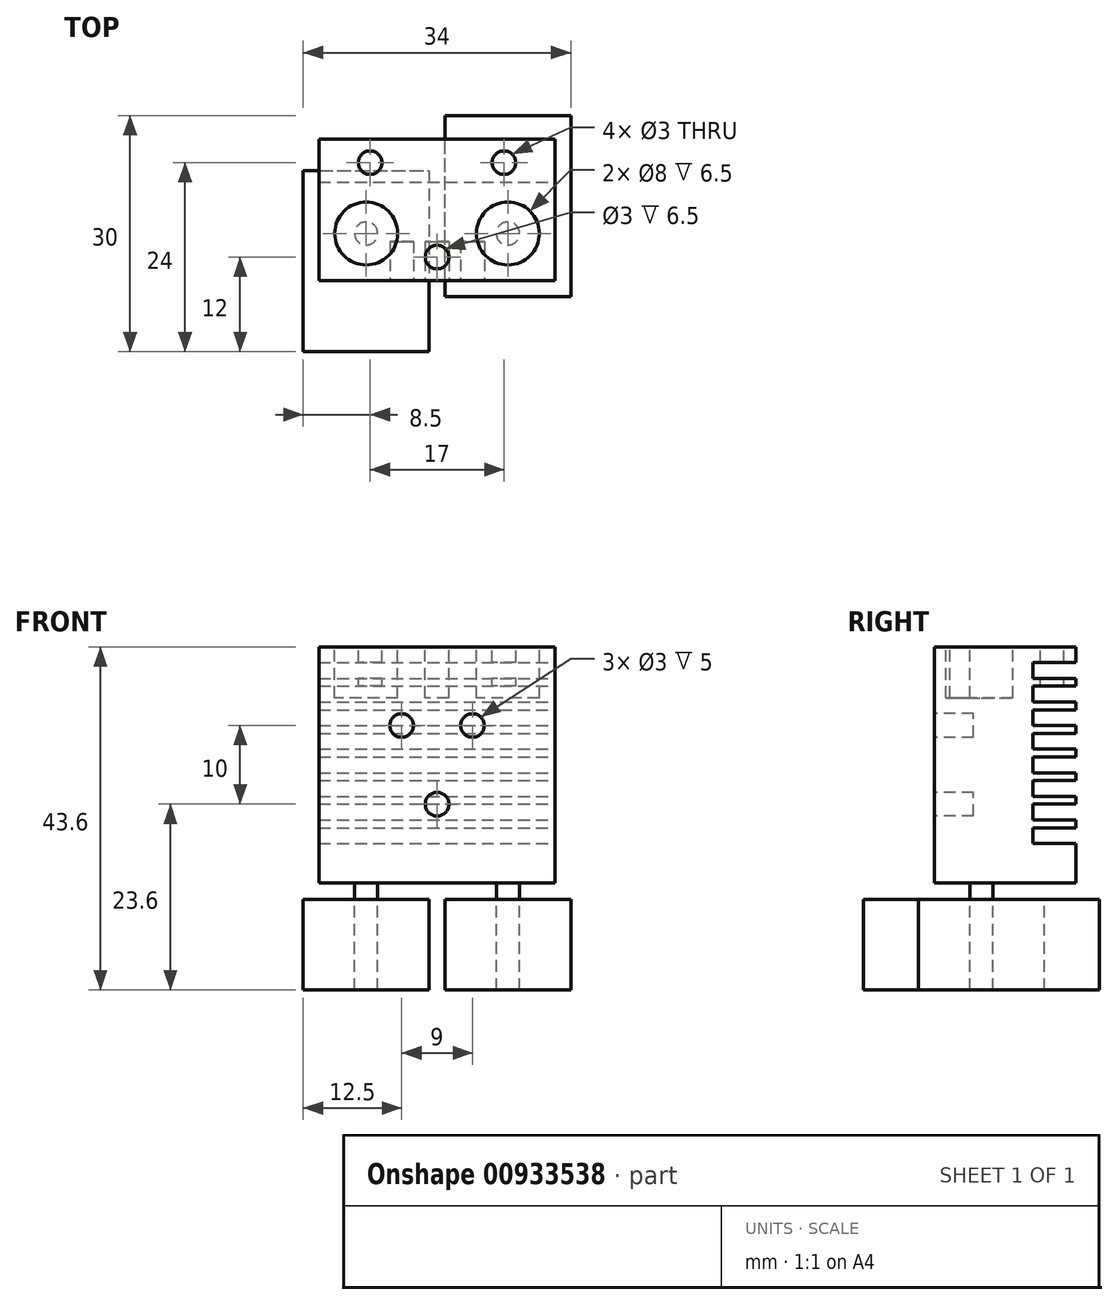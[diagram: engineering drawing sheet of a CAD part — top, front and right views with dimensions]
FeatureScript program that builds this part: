
annotation { "Feature Type Name" : "Feature", "Feature Type Description" : "" }
export const myFeature = defineFeature(function(context is Context, id is Id, definition is map)
    precondition{}
    {
        {
            var Q0;
            Q0=qCreatedBy(makeId("Front.planeOp"),FACE);
            var sketch = newSketch(context, id + "F0", { "sketchPlane" : qUnion([Q0])});
            skLineSegment(sketch, "E0.bottom", {"start": v(0, 0) * mm, "end": v(30, 0) * mm});
            skLineSegment(sketch, "E0.top", {"start": v(0, -30) * mm, "end": v(30, -30) * mm});
            skLineSegment(sketch, "E0.left", {"start": v(0, 0) * mm, "end": v(0, -30) * mm});
            skLineSegment(sketch, "E0.right", {"start": v(30, 0) * mm, "end": v(30, -30) * mm});
            skSolve(sketch);
        }
        {
            var Q0;
            Q0 = qSketchRegion(id + "F0", true);
            extrude(context, id + "F1", {"entities" : qUnion([Q0]), "depth" : 18 * mm, "offsetDistance" : 25 * mm});
        }
        {
            var Q0;
            Q0=makeQuery(id+"F1.opExtrude","SWEPT_FACE",FACE,{"disambiguationData":[OSD([sQuery(id+"F0.wireOp",EDGE,"E0.bottom")])]});
            var sketch = newSketch(context, id + "F2", { "sketchPlane" : qUnion([Q0])});
            skLineSegment(sketch, "E1", {"start": v(0, -18) * mm, "end": v(6, -18) * mm, "construction": true});
            skLineSegment(sketch, "E2", {"start": v(6, -18) * mm, "end": v(6, -12) * mm, "construction": true});
            skLineSegment(sketch, "E3", {"start": v(30, -18) * mm, "end": v(24, -18) * mm, "construction": true});
            skLineSegment(sketch, "E4", {"start": v(24, -18) * mm, "end": v(24, -12) * mm, "construction": true});
            skLineSegment(sketch, "E5", {"start": v(15, -18) * mm, "end": v(15, -15) * mm, "construction": true});
            skLineSegment(sketch, "E6", {"start": v(15, 0) * mm, "end": v(15, -3) * mm, "construction": true});
            skLineSegment(sketch, "E7", {"start": v(30, -3) * mm, "end": v(23.5, -3) * mm, "construction": true});
            skLineSegment(sketch, "E8", {"start": v(0, -3) * mm, "end": v(6.5, -3) * mm, "construction": true});
            skCircle(sketch, "E9", {"center": v(24, -12) * mm, "radius": 4 * mm});
            skCircle(sketch, "E10", {"center": v(6, -12) * mm, "radius": 4 * mm});
            skCircle(sketch, "E11", {"center": v(6.5, -3) * mm, "radius": 1.5 * mm});
            skCircle(sketch, "E12", {"center": v(23.5, -3) * mm, "radius": 1.5 * mm});
            skCircle(sketch, "E13", {"center": v(15, -15) * mm, "radius": 1.5 * mm});
            skSolve(sketch);
        }
        {
            var Q0;
            Q0=makeQuery(id+"F2.imprint","IMPRINT",FACE,{"disambiguationData":[TD([[makeQuery(id+"F2.imprint","IMPRINT",EDGE,{"derivedFrom":sQuery(id+"F2.wireOp",EDGE,"E10")}),1.0]])]});
            var Q1;
            Q1=makeQuery(id+"F2.imprint","IMPRINT",FACE,{"disambiguationData":[TD([[makeQuery(id+"F2.imprint","IMPRINT",EDGE,{"derivedFrom":sQuery(id+"F2.wireOp",EDGE,"E9")}),1.0]])]});
            var Q2;
            Q2=makeQuery(id+"F2.imprint","IMPRINT",FACE,{"disambiguationData":[TD([[makeQuery(id+"F2.imprint","IMPRINT",EDGE,{"derivedFrom":sQuery(id+"F2.wireOp",EDGE,"E11")}),1.0]])]});
            var Q3;
            Q3=makeQuery(id+"F2.imprint","IMPRINT",FACE,{"disambiguationData":[TD([[makeQuery(id+"F2.imprint","IMPRINT",EDGE,{"derivedFrom":sQuery(id+"F2.wireOp",EDGE,"E12")}),1.0]])]});
            var Q4;
            Q4=makeQuery(id+"F2.imprint","IMPRINT",FACE,{"disambiguationData":[TD([[makeQuery(id+"F2.imprint","IMPRINT",EDGE,{"derivedFrom":sQuery(id+"F2.wireOp",EDGE,"E13")}),1.0]])]});
            extrude(context, id + "F3", {"entities" : qUnion([Q0, Q1, Q2, Q3, Q4]), "operationType" : NewBodyOperationType.REMOVE, "oppositeDirection" : true, "depth" : 6.5 * mm, "offsetDistance" : 25 * mm});
        }
        {
            var Q0;
            Q0=makeQuery(id+"F1.opExtrude","CAP_FACE",FACE,{"disambiguationData":[OSD([sQuery(id+"F0.wireOp",EDGE,"E0.bottom"),sQuery(id+"F0.wireOp",EDGE,"E0.top"),sQuery(id+"F0.wireOp",EDGE,"E0.left"),sQuery(id+"F0.wireOp",EDGE,"E0.right")])],"isStart":false});
            var sketch = newSketch(context, id + "F4", { "sketchPlane" : qUnion([Q0])});
            skLineSegment(sketch, "E14", {"start": v(15, -30) * mm, "end": v(15, -20) * mm, "construction": true});
            skLineSegment(sketch, "E15", {"start": v(0, -30) * mm, "end": v(0, -10) * mm, "construction": true});
            skLineSegment(sketch, "E16", {"start": v(0, -10) * mm, "end": v(10.5, -10) * mm, "construction": true});
            skLineSegment(sketch, "E17", {"start": v(10.5, -10) * mm, "end": v(19.5, -10) * mm, "construction": true});
            skCircle(sketch, "E18", {"center": v(10.5, -10) * mm, "radius": 1.5 * mm});
            skCircle(sketch, "E19", {"center": v(19.5, -10) * mm, "radius": 1.5 * mm});
            skCircle(sketch, "E20", {"center": v(15, -20) * mm, "radius": 1.5 * mm});
            skSolve(sketch);
        }
        {
            var Q0;
            Q0=makeQuery(id+"F4.imprint","IMPRINT",FACE,{"disambiguationData":[TD([[makeQuery(id+"F4.imprint","IMPRINT",EDGE,{"derivedFrom":sQuery(id+"F4.wireOp",EDGE,"E19")}),1.0]])]});
            var Q1;
            Q1=makeQuery(id+"F4.imprint","IMPRINT",FACE,{"disambiguationData":[TD([[makeQuery(id+"F4.imprint","IMPRINT",EDGE,{"derivedFrom":sQuery(id+"F4.wireOp",EDGE,"E20")}),1.0]])]});
            var Q2;
            Q2=makeQuery(id+"F4.imprint","IMPRINT",FACE,{"disambiguationData":[TD([[makeQuery(id+"F4.imprint","IMPRINT",EDGE,{"derivedFrom":sQuery(id+"F4.wireOp",EDGE,"E18")}),1.0]])]});
            extrude(context, id + "F5", {"entities" : qUnion([Q0, Q1, Q2]), "operationType" : NewBodyOperationType.REMOVE, "oppositeDirection" : true, "depth" : 5 * mm, "offsetDistance" : 25 * mm});
        }
        {
            var Q0;
            Q0=makeQuery(id+"F1.opExtrude","SWEPT_FACE",FACE,{"disambiguationData":[OSD([sQuery(id+"F0.wireOp",EDGE,"E0.right")])]});
            var sketch = newSketch(context, id + "F6", { "sketchPlane" : qUnion([Q0])});
            skLineSegment(sketch, "E21", {"start": v(0, 0) * mm, "end": v(0, -2) * mm, "construction": true});
            skLineSegment(sketch, "E22", {"start": v(0, -2) * mm, "end": v(0, -4) * mm, "construction": true});
            skLineSegment(sketch, "E23", {"start": v(0, -4) * mm, "end": v(0, -5) * mm, "construction": true});
            skLineSegment(sketch, "E24", {"start": v(0, -5) * mm, "end": v(0, -7) * mm, "construction": true});
            skLineSegment(sketch, "E25", {"start": v(0, -7) * mm, "end": v(0, -8) * mm, "construction": true});
            skLineSegment(sketch, "E26", {"start": v(0, -8) * mm, "end": v(0, -10) * mm, "construction": true});
            skLineSegment(sketch, "E27", {"start": v(0, -10) * mm, "end": v(0, -11) * mm, "construction": true});
            skLineSegment(sketch, "E28", {"start": v(0, -11) * mm, "end": v(0, -13) * mm, "construction": true});
            skLineSegment(sketch, "E29", {"start": v(0, -13) * mm, "end": v(0, -14) * mm, "construction": true});
            skLineSegment(sketch, "E30", {"start": v(0, -14) * mm, "end": v(0, -16) * mm, "construction": true});
            skLineSegment(sketch, "E31", {"start": v(0, -16) * mm, "end": v(0, -17) * mm, "construction": true});
            skLineSegment(sketch, "E32", {"start": v(0, -17) * mm, "end": v(0, -19) * mm, "construction": true});
            skLineSegment(sketch, "E33", {"start": v(0, -19) * mm, "end": v(0, -20) * mm, "construction": true});
            skLineSegment(sketch, "E34", {"start": v(0, -20) * mm, "end": v(0, -22) * mm, "construction": true});
            skLineSegment(sketch, "E35", {"start": v(0, -22) * mm, "end": v(0, -23) * mm, "construction": true});
            skLineSegment(sketch, "E36", {"start": v(0, -23) * mm, "end": v(0, -25) * mm, "construction": true});
            skLineSegment(sketch, "E37", {"start": v(0, -25) * mm, "end": v(0, -26) * mm, "construction": true});
            skLineSegment(sketch, "E38", {"start": v(0, -26) * mm, "end": v(0, -28) * mm, "construction": true});
            skLineSegment(sketch, "E39", {"start": v(0, 0) * mm, "end": v(-5.5, 0) * mm, "construction": true});
            skLineSegment(sketch, "E40.bottom", {"start": v(0, -2) * mm, "end": v(-5.5, -2) * mm});
            skLineSegment(sketch, "E40.top", {"start": v(0, -4) * mm, "end": v(-5.5, -4) * mm});
            skLineSegment(sketch, "E40.left", {"start": v(0, -2) * mm, "end": v(0, -4) * mm});
            skLineSegment(sketch, "E40.right", {"start": v(-5.5, -2) * mm, "end": v(-5.5, -4) * mm});
            skLineSegment(sketch, "E41.bottom", {"start": v(0, -5) * mm, "end": v(-5.5, -5) * mm});
            skLineSegment(sketch, "E41.top", {"start": v(0, -7) * mm, "end": v(-5.5, -7) * mm});
            skLineSegment(sketch, "E41.left", {"start": v(0, -5) * mm, "end": v(0, -7) * mm});
            skLineSegment(sketch, "E41.right", {"start": v(-5.5, -5) * mm, "end": v(-5.5, -7) * mm});
            skLineSegment(sketch, "E42.bottom", {"start": v(0, -8) * mm, "end": v(-5.5, -8) * mm});
            skLineSegment(sketch, "E42.top", {"start": v(0, -10) * mm, "end": v(-5.5, -10) * mm});
            skLineSegment(sketch, "E42.left", {"start": v(0, -8) * mm, "end": v(0, -10) * mm});
            skLineSegment(sketch, "E42.right", {"start": v(-5.5, -8) * mm, "end": v(-5.5, -10) * mm});
            skLineSegment(sketch, "E43.bottom", {"start": v(0, -11) * mm, "end": v(-5.5, -11) * mm});
            skLineSegment(sketch, "E43.top", {"start": v(0, -13) * mm, "end": v(-5.5, -13) * mm});
            skLineSegment(sketch, "E43.left", {"start": v(0, -11) * mm, "end": v(0, -13) * mm});
            skLineSegment(sketch, "E43.right", {"start": v(-5.5, -11) * mm, "end": v(-5.5, -13) * mm});
            skLineSegment(sketch, "E44.bottom", {"start": v(0, -14) * mm, "end": v(-5.5, -14) * mm});
            skLineSegment(sketch, "E44.top", {"start": v(0, -16) * mm, "end": v(-5.5, -16) * mm});
            skLineSegment(sketch, "E44.left", {"start": v(0, -14) * mm, "end": v(0, -16) * mm});
            skLineSegment(sketch, "E44.right", {"start": v(-5.5, -14) * mm, "end": v(-5.5, -16) * mm});
            skLineSegment(sketch, "E45.bottom", {"start": v(0, -17) * mm, "end": v(-5.5, -17) * mm});
            skLineSegment(sketch, "E45.top", {"start": v(0, -19) * mm, "end": v(-5.5, -19) * mm});
            skLineSegment(sketch, "E45.left", {"start": v(0, -17) * mm, "end": v(0, -19) * mm});
            skLineSegment(sketch, "E45.right", {"start": v(-5.5, -17) * mm, "end": v(-5.5, -19) * mm});
            skLineSegment(sketch, "E46.bottom", {"start": v(0, -20) * mm, "end": v(-5.5, -20) * mm});
            skLineSegment(sketch, "E46.top", {"start": v(0, -22) * mm, "end": v(-5.5, -22) * mm});
            skLineSegment(sketch, "E46.left", {"start": v(0, -20) * mm, "end": v(0, -22) * mm});
            skLineSegment(sketch, "E46.right", {"start": v(-5.5, -20) * mm, "end": v(-5.5, -22) * mm});
            skLineSegment(sketch, "E47.bottom", {"start": v(0, -23) * mm, "end": v(-5.5, -23) * mm});
            skLineSegment(sketch, "E47.top", {"start": v(0, -25) * mm, "end": v(-5.5, -25) * mm});
            skLineSegment(sketch, "E47.left", {"start": v(0, -23) * mm, "end": v(0, -25) * mm});
            skLineSegment(sketch, "E47.right", {"start": v(-5.5, -23) * mm, "end": v(-5.5, -25) * mm});
            skLineSegment(sketch, "E48.bottom", {"start": v(0, -26) * mm, "end": v(-5.5, -26) * mm});
            skLineSegment(sketch, "E48.top", {"start": v(0, -28) * mm, "end": v(-5.5, -28) * mm});
            skLineSegment(sketch, "E48.left", {"start": v(0, -26) * mm, "end": v(0, -28) * mm});
            skLineSegment(sketch, "E48.right", {"start": v(-5.5, -26) * mm, "end": v(-5.5, -28) * mm});
            skSolve(sketch);
        }
        {
            var Q0;
            Q0=makeQuery(id+"F6.imprint","IMPRINT",FACE,{"disambiguationData":[TD([[makeQuery(id+"F6.imprint","IMPRINT",EDGE,{"derivedFrom":sQuery(id+"F6.wireOp",EDGE,"E40.bottom")}),1.0]])]});
            var Q1;
            Q1=makeQuery(id+"F6.imprint","IMPRINT",FACE,{"disambiguationData":[TD([[makeQuery(id+"F6.imprint","IMPRINT",EDGE,{"derivedFrom":sQuery(id+"F6.wireOp",EDGE,"E41.bottom")}),1.0]])]});
            var Q2;
            Q2=makeQuery(id+"F6.imprint","IMPRINT",FACE,{"disambiguationData":[TD([[makeQuery(id+"F6.imprint","IMPRINT",EDGE,{"derivedFrom":sQuery(id+"F6.wireOp",EDGE,"E42.bottom")}),1.0]])]});
            var Q3;
            Q3=makeQuery(id+"F6.imprint","IMPRINT",FACE,{"disambiguationData":[TD([[makeQuery(id+"F6.imprint","IMPRINT",EDGE,{"derivedFrom":sQuery(id+"F6.wireOp",EDGE,"E43.bottom")}),1.0]])]});
            var Q4;
            Q4=makeQuery(id+"F6.imprint","IMPRINT",FACE,{"disambiguationData":[TD([[makeQuery(id+"F6.imprint","IMPRINT",EDGE,{"derivedFrom":sQuery(id+"F6.wireOp",EDGE,"E44.bottom")}),1.0]])]});
            var Q5;
            Q5=makeQuery(id+"F6.imprint","IMPRINT",FACE,{"disambiguationData":[TD([[makeQuery(id+"F6.imprint","IMPRINT",EDGE,{"derivedFrom":sQuery(id+"F6.wireOp",EDGE,"E45.bottom")}),1.0]])]});
            var Q6;
            Q6=makeQuery(id+"F6.imprint","IMPRINT",FACE,{"disambiguationData":[TD([[makeQuery(id+"F6.imprint","IMPRINT",EDGE,{"derivedFrom":sQuery(id+"F6.wireOp",EDGE,"E46.bottom")}),1.0]])]});
            var Q7;
            Q7=makeQuery(id+"F6.imprint","IMPRINT",FACE,{"disambiguationData":[TD([[makeQuery(id+"F6.imprint","IMPRINT",EDGE,{"derivedFrom":sQuery(id+"F6.wireOp",EDGE,"E47.bottom")}),1.0]])]});
            var Q8;
            Q8=makeQuery(id+"F1.opExtrude","SWEPT_FACE",FACE,{"disambiguationData":[OSD([sQuery(id+"F0.wireOp",EDGE,"E0.left")])]});
            extrude(context, id + "F7", {"entities" : qUnion([Q0, Q1, Q2, Q3, Q4, Q5, Q6, Q7]), "operationType" : NewBodyOperationType.REMOVE, "endBound" : BoundingType.UP_TO_SURFACE, "oppositeDirection" : true, "depth" : 25 * mm, "endBoundEntityFace" : qUnion([Q8]), "offsetDistance" : 25 * mm});
        }
        {
            var Q0;
            Q0=makeQuery(id+"F1.opExtrude","SWEPT_FACE",FACE,{"disambiguationData":[OSD([sQuery(id+"F0.wireOp",EDGE,"E0.top")])]});
            var sketch = newSketch(context, id + "F8", { "sketchPlane" : qUnion([Q0])});
            skLineSegment(sketch, "E49", {"start": v(0, 18) * mm, "end": v(6, 18) * mm, "construction": true});
            skLineSegment(sketch, "E50", {"start": v(6, 18) * mm, "end": v(6, 12) * mm, "construction": true});
            skLineSegment(sketch, "E51", {"start": v(30, 18) * mm, "end": v(24, 18) * mm, "construction": true});
            skLineSegment(sketch, "E52", {"start": v(24, 18) * mm, "end": v(24, 12) * mm, "construction": true});
            skCircle(sketch, "E53", {"center": v(6, 12) * mm, "radius": 1.48 * mm});
            skCircle(sketch, "E54", {"center": v(24, 12) * mm, "radius": 1.48 * mm});
            skSolve(sketch);
        }
        {
            var Q0;
            Q0=makeQuery(id+"F8.imprint","IMPRINT",FACE,{"disambiguationData":[TD([[makeQuery(id+"F8.imprint","IMPRINT",EDGE,{"derivedFrom":sQuery(id+"F8.wireOp",EDGE,"E53")}),1.0]])]});
            var Q1;
            Q1=makeQuery(id+"F8.imprint","IMPRINT",FACE,{"disambiguationData":[TD([[makeQuery(id+"F8.imprint","IMPRINT",EDGE,{"derivedFrom":sQuery(id+"F8.wireOp",EDGE,"E54")}),1.0]])]});
            extrude(context, id + "F9", {"entities" : qUnion([Q0, Q1]), "depth" : 2.1 * mm, "offsetDistance" : 25 * mm});
        }
        {
            var Q0;
            Q0=makeQuery(id+"F9.opExtrude","CAP_FACE",FACE,{"disambiguationData":[OSD([sQuery(id+"F8.wireOp",EDGE,"E54")])],"isStart":false});
            var sketch = newSketch(context, id + "F10", { "sketchPlane" : qUnion([Q0])});
            skLineSegment(sketch, "E55", {"start": v(24, 12) * mm, "end": v(32, 12) * mm, "construction": true});
            skLineSegment(sketch, "E56", {"start": v(32, 12) * mm, "end": v(32, 20) * mm, "construction": true});
            skLineSegment(sketch, "E57.bottom", {"start": v(32, 20) * mm, "end": v(16, 20) * mm});
            skLineSegment(sketch, "E57.top", {"start": v(32, -3) * mm, "end": v(16, -3) * mm});
            skLineSegment(sketch, "E57.left", {"start": v(32, 20) * mm, "end": v(32, -3) * mm});
            skLineSegment(sketch, "E57.right", {"start": v(16, 20) * mm, "end": v(16, -3) * mm});
            skSolve(sketch);
        }
        {
            var Q0;
            Q0=makeQuery(id+"F9.opExtrude","CAP_FACE",FACE,{"disambiguationData":[OSD([sQuery(id+"F8.wireOp",EDGE,"E53")])],"isStart":false});
            var sketch = newSketch(context, id + "F11", { "sketchPlane" : qUnion([Q0])});
            skLineSegment(sketch, "E58", {"start": v(6, 12) * mm, "end": v(6, 4) * mm, "construction": true});
            skLineSegment(sketch, "E59", {"start": v(6, 4) * mm, "end": v(-2, 4) * mm, "construction": true});
            skLineSegment(sketch, "E60.bottom", {"start": v(-2, 4) * mm, "end": v(14, 4) * mm});
            skLineSegment(sketch, "E60.top", {"start": v(-2, 27) * mm, "end": v(14, 27) * mm});
            skLineSegment(sketch, "E60.left", {"start": v(-2, 4) * mm, "end": v(-2, 27) * mm});
            skLineSegment(sketch, "E60.right", {"start": v(14, 4) * mm, "end": v(14, 27) * mm});
            skSolve(sketch);
        }
        {
            var Q0;
            Q0=makeQuery(id+"F10.imprint","IMPRINT",FACE,{"disambiguationData":[TD([[makeQuery(id+"F10.imprint","IMPRINT",EDGE,{"derivedFrom":sQuery(id+"F10.wireOp",EDGE,"E57.bottom")}),1.0]])]});
            var Q1;
            Q1=makeQuery(id+"F11.imprint","IMPRINT",FACE,{"disambiguationData":[TD([[makeQuery(id+"F11.imprint","IMPRINT",EDGE,{"derivedFrom":sQuery(id+"F11.wireOp",EDGE,"E60.bottom")}),1.0]])]});
            extrude(context, id + "F12", {"entities" : qUnion([Q0, Q1]), "depth" : 11.5 * mm, "offsetDistance" : 25 * mm});
        }
    });
